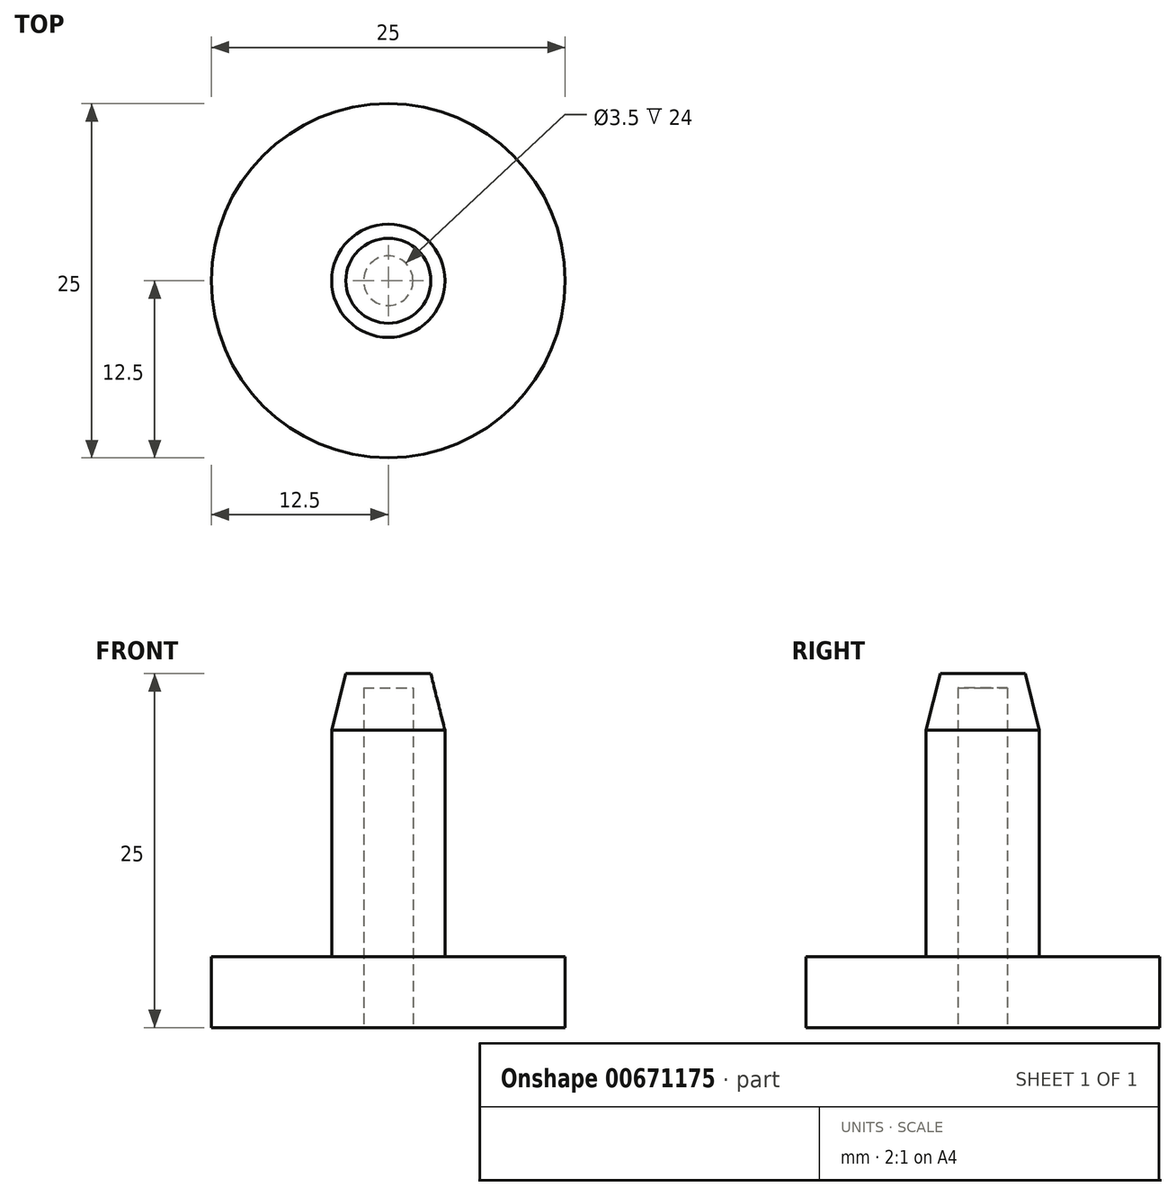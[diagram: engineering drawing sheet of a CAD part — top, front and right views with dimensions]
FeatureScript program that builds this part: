
annotation { "Feature Type Name" : "Feature", "Feature Type Description" : "" }
export const myFeature = defineFeature(function(context is Context, id is Id, definition is map)
    precondition{}
    {
        {
            var Q0;
            Q0=qCreatedBy(makeId("Top.planeOp"),FACE);
            var sketch = newSketch(context, id + "F0", { "sketchPlane" : qUnion([Q0])});
            skCircle(sketch, "E0", {"center": v(0, 0) * mm, "radius": 12.5 * mm});
            skSolve(sketch);
        }
        {
            var Q0;
            Q0 = qSketchRegion(id + "F0", true);
            extrude(context, id + "F1", {"entities" : qUnion([Q0]), "depth" : 5 * mm, "offsetDistance" : 25 * mm});
        }
        {
            var Q0;
            Q0=makeQuery(id+"F1.opExtrude","CAP_FACE",FACE,{"disambiguationData":[OSD([sQuery(id+"F0.wireOp",EDGE,"E0")])],"isStart":false});
            var sketch = newSketch(context, id + "F2", { "sketchPlane" : qUnion([Q0])});
            skCircle(sketch, "E1", {"center": v(0, 0) * mm, "radius": 4 * mm});
            skSolve(sketch);
        }
        {
            var Q0;
            Q0 = qSketchRegion(id + "F2", true);
            extrude(context, id + "F3", {"entities" : qUnion([Q0]), "operationType" : NewBodyOperationType.ADD, "depth" : 20 * mm, "offsetDistance" : 25 * mm});
        }
        {
            var Q0;
            Q0=makeQuery(id+"F3.opExtrude","CAP_EDGE",EDGE,{"disambiguationData":[OSD([sQuery(id+"F2.wireOp",EDGE,"E1")])],"isStart":false});
            chamfer(context, id + "F4", {"entities" : qUnion([Q0]), "chamferType" : ChamferType.TWO_OFFSETS, "width1" : 1 * mm, "oppositeDirection" : false, "width2" : 4 * mm, "tangentPropagation" : true});
        }
        {
            var Q0;
            Q0=makeQuery(id+"F1.opExtrude","CAP_FACE",FACE,{"disambiguationData":[OSD([sQuery(id+"F0.wireOp",EDGE,"E0")])],"isStart":true});
            var sketch = newSketch(context, id + "F5", { "sketchPlane" : qUnion([Q0])});
            skCircle(sketch, "E2", {"center": v(0, 0) * mm, "radius": 1.75 * mm});
            skSolve(sketch);
        }
        {
            var Q0;
            Q0 = qSketchRegion(id + "F5", true);
            extrude(context, id + "F6", {"entities" : qUnion([Q0]), "operationType" : NewBodyOperationType.REMOVE, "oppositeDirection" : true, "depth" : 24 * mm, "offsetDistance" : 25 * mm});
        }
    });
